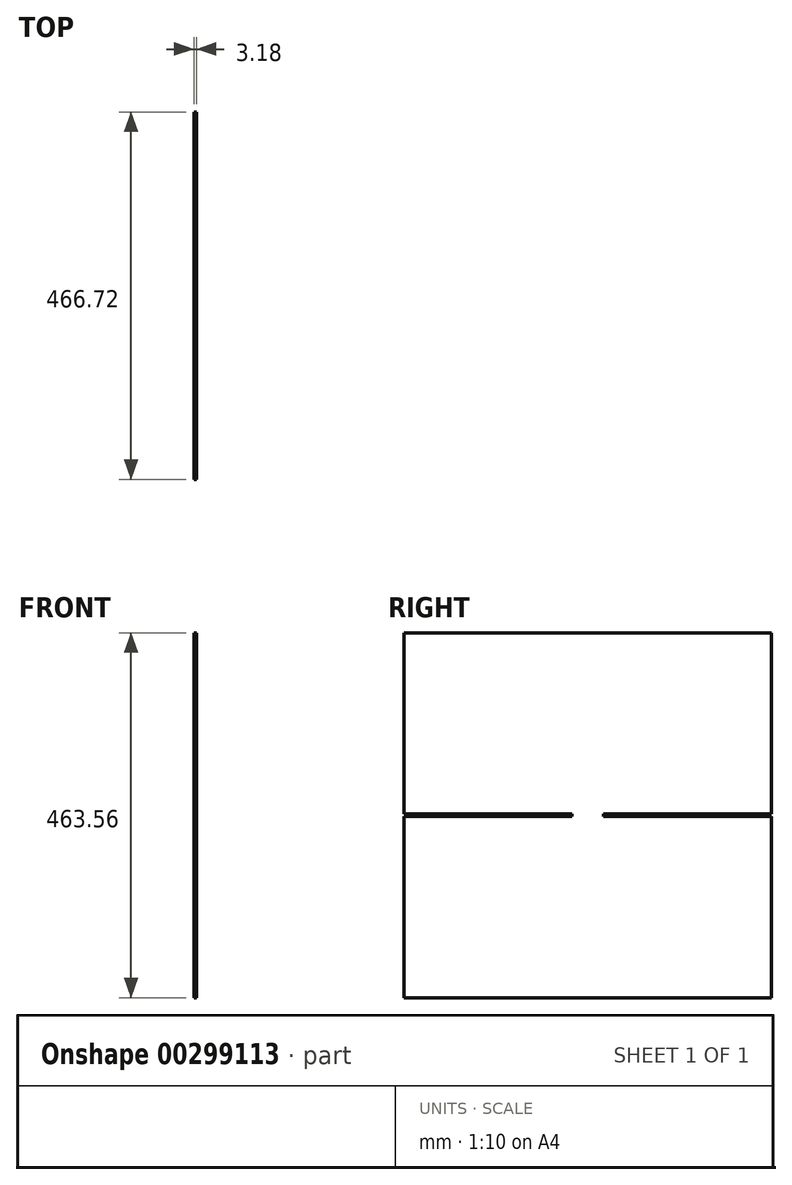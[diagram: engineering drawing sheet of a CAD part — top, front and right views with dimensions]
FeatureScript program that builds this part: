
annotation { "Feature Type Name" : "Feature", "Feature Type Description" : "" }
export const myFeature = defineFeature(function(context is Context, id is Id, definition is map)
    precondition{}
    {
        {
            var Q0;
            Q0=qCreatedBy(makeId("Top.planeOp"),FACE);
            var sketch = newSketch(context, id + "F0", { "sketchPlane" : qUnion([Q0])});
            skLineSegment(sketch, "E0.bottom", {"start": v(1.59, 233.36) * mm, "end": v(-1.59, 233.36) * mm});
            skLineSegment(sketch, "E0.top", {"start": v(1.59, -233.36) * mm, "end": v(-1.59, -233.36) * mm});
            skLineSegment(sketch, "E0.left", {"start": v(1.59, 233.36) * mm, "end": v(1.59, -233.36) * mm});
            skLineSegment(sketch, "E0.right", {"start": v(-1.59, 233.36) * mm, "end": v(-1.59, -233.36) * mm});
            skPoint(sketch, "E0.middle", {"position": v(0, 0) * mm});
            skSolve(sketch);
        }
        {
            var Q0;
            Q0 = qSketchRegion(id + "F0", true);
            extrude(context, id + "F1", {"entities" : qUnion([Q0]), "endBound" : BoundingType.SYMMETRIC, "depth" : 463.55 * mm});
        }
        {
            var Q0;
            Q0=makeQuery(id+"F1.opExtrude","SWEPT_FACE",FACE,{"disambiguationData":[OSD([sQuery(id+"F0.wireOp",EDGE,"E0.left")])]});
            var sketch = newSketch(context, id + "F2", { "sketchPlane" : qUnion([Q0])});
            skLineSegment(sketch, "E1", {"start": v(-19.84, 0) * mm, "end": v(-233.36, 0) * mm, "construction": true});
            skLineSegment(sketch, "E2", {"start": v(0, -31.19) * mm, "end": v(0, 31.5) * mm, "construction": true});
            skLineSegment(sketch, "E3", {"start": v(-19.84, 0) * mm, "end": v(-19.84, 1.59) * mm, "construction": true});
            skLineSegment(sketch, "E4", {"start": v(-19.84, 36.89) * mm, "end": v(-19.84, 18.44) * mm, "construction": true});
            skPoint(sketch, "E4.endSnap0", {"position": v(-19.84, 18.44) * mm});
            skPoint(sketch, "E5.orphan", {"position": v(0, 0) * mm});
            skLineSegment(sketch, "E6.bottom", {"start": v(-233.36, 1.59) * mm, "end": v(-19.84, 1.59) * mm});
            skLineSegment(sketch, "E6.top", {"start": v(-233.36, -1.59) * mm, "end": v(-19.84, -1.59) * mm});
            skLineSegment(sketch, "E6.left", {"start": v(-233.36, 1.59) * mm, "end": v(-233.36, -1.59) * mm});
            skLineSegment(sketch, "E6.right", {"start": v(-19.84, 1.59) * mm, "end": v(-19.84, -1.59) * mm});
            skPoint(sketch, "E6.middle", {"position": v(-126.6, 0) * mm});
            skLineSegment(sketch, "E7.trimOffspring", {"start": v(-19.84, 1.59) * mm, "end": v(-19.84, -1.59) * mm, "construction": true});
            skLineSegment(sketch, "E8.trimOffspring", {"start": v(-19.84, 18.44) * mm, "end": v(-19.84, 36.89) * mm, "construction": true});
            skPoint(sketch, "E9.orphan", {"position": v(-19.84, -33.5) * mm});
            skLineSegment(sketch, "E10.MirrorCS", {"start": v(19.84, 1.59) * mm, "end": v(19.84, -1.59) * mm, "construction": true});
            skLineSegment(sketch, "E11.MirrorCS", {"start": v(233.36, -1.59) * mm, "end": v(19.84, -1.59) * mm});
            skLineSegment(sketch, "E12.MirrorCS", {"start": v(19.84, 0) * mm, "end": v(19.84, 1.59) * mm, "construction": true});
            skLineSegment(sketch, "E13.MirrorCS", {"start": v(233.36, 1.59) * mm, "end": v(19.84, 1.59) * mm});
            skLineSegment(sketch, "E14.MirrorCS", {"start": v(233.36, 1.59) * mm, "end": v(233.36, -1.59) * mm});
            skLineSegment(sketch, "E15", {"start": v(19.84, 1.59) * mm, "end": v(19.84, -1.59) * mm});
            skSolve(sketch);
        }
        {
            var Q0;
            Q0 = qSketchRegion(id + "F2", true);
            extrude(context, id + "F3", {"entities" : qUnion([Q0]), "operationType" : NewBodyOperationType.REMOVE, "endBound" : BoundingType.THROUGH_ALL, "oppositeDirection" : true, "depth" : 25.4 * mm});
        }
    });
